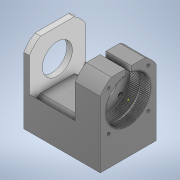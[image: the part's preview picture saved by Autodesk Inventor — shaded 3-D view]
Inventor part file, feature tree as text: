
AUTODESK INVENTOR PART (.ipt)
format: ipt  version: 2022 (Build 260153000, 153)  size: 1,474,560 bytes
history: mixed  units: mm
features: other x3, sketch x3, extrude x2, imported_body x1
ambient origin geometry x8: Origin, YZ Plane, XZ Plane, XY Plane, X Axis, Y Axis, Z Axis, Center Point
bodies: Solid1 (imported_parasolid)
feature tree (9):
  other  "Assembly2.iam"
  other  "96Gears_Stage_1_modified.ipt:1"
  other  "96Gears_Stage_2_modified.ipt:1"
  extrude  "Extrusion3"  Depth=3.0mm
  extrude  "Extrusion5"  Depth=6.0mm TaperAngle=0.0deg
  sketch  "Sketch5"  dims[d7=6.0mm d8=18.0mm d9=0.0mm]
  sketch  "Sketch4"  dims[d0=10.0mm d6=3.0mm]
  sketch  "Sketch7"  dims[d17=32.25mm d18=6.0mm d19=0.0mm]
  imported_body  NMx_Import_Brep_tag  [imported B-rep: ~787 faces, bbox_mm=[82.0, 83.027756, 60.0]]
